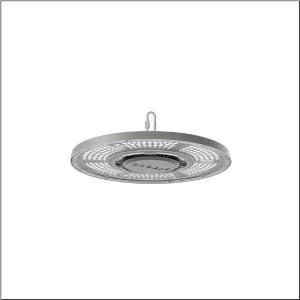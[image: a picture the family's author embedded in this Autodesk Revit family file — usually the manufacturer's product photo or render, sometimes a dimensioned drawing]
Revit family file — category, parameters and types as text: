
# Revit family: highbay_31-s_51hc417a4fmb
name_source: partatom
category: Lighting Fixtures
units: mm (PartAtom-declared; Revit-internal decimal feet)

## family parameters
Cut with Voids When Loaded = No
Host = Face
Light Source = No
Part Type = Normal
Room Calculation Point = No
Round Connector Dimension = Use Diameter
Shared = No

## types (1)
- Highbay 31-S (1 x LED, 14000 lm, 94 W, 4000K)
    Apparent Load = 94 VA
    CIE Flux Codes = 94 98 100 100 100
    Color Rendering = 80
    Color Temperature = 4000K
    Default Elevation = 1800 mm
    Description = Highbay 31-S, LED high bay luminaire, primary light control with lens, of PC, primary optical cover: cover panel, of PC, transparent, light emission: direct distribution, primary light characteristic: rotationally symmetric, installation type: suspended mounting, surface-mounted, LED, rated luminous flux: 14.000lm, luminous efficacy: 150lm/W, light colour: 840, colour temperature: 4000K, control gear: ECG, with cable, 3x 1.0mm², free wire ends, mains connection: 220..240V, AC/DC, 0/50..60Hz, cable length: 1,5m, rated input power: 94W, housing, rotationally symmetric, of diecast aluminium, powder-coated, grey aluminium (RAL 9007), with hook on luminaire side, incl. screw, diameter: 339mm, protection rating (complete): IP65, insulation class (complete): insulation class I (protective earthing), certification: CE, ENEC, UKCA, protection symbol: D, impact resistance: IK08, permissible operating ambient temperature: -30..+45°C, standard: EN 60598-2-22, EN 60598, corresponds to IFS (International Featured Standards) requirements for safety and quality in the food industry, packaging unit: 1 piece
    Height = 141 mm
    Lamp = 1 x LED
    Lamp Light Flux = 14000 lm
    Lamp Power = 94 W
    Lamp count = 1
    Length = 339 mm
    Luminous efficacy = 149 lm/W
    Manufacturer = Siteco
    ModVariant = No
    Model = 51HC417A4FMB
    Mounting Place = Ceiling
    Mounting Type = Pendant
    Number of Poles = 1
    OnlyDefault = Yes
    Power Factor = 1
    Product Name = Highbay 31-S
    Product group = LED high bay luminaire
    ProductGroupID = 903
    Protection Class = Protection class I
    Protection Degree = IP 65
    RLX_Detail_Level = 1
    RLX_Emergency_Light_Flux = 0 lm
    RLX_Emergency_Type = 0
    RLX_Emergency_Type_DB = No
    RlxData = <blob elided: 106477 chars, md5=9952910f>
    Socket = socket
    Standby Power = 0 W
    System Light Flux = 14000 lm
    System Power = 94 W
    Type Comments = Product without accessories
    Type Image = l_1007237.jpg
    URL = http://relux.com
    VarID = ---
    Voltage = 0 V
    Weight = 0.00 kg
    Width = 0 mm  [stored 0 ft]

note: [stored X ft] marks values corroborated as IEEE doubles in the binary element streams (Revit-internal decimal feet)

## geometry (parser evidence)
native form markers: Blend x4, Sweep x8
no freeform markers — native parametric forms only
